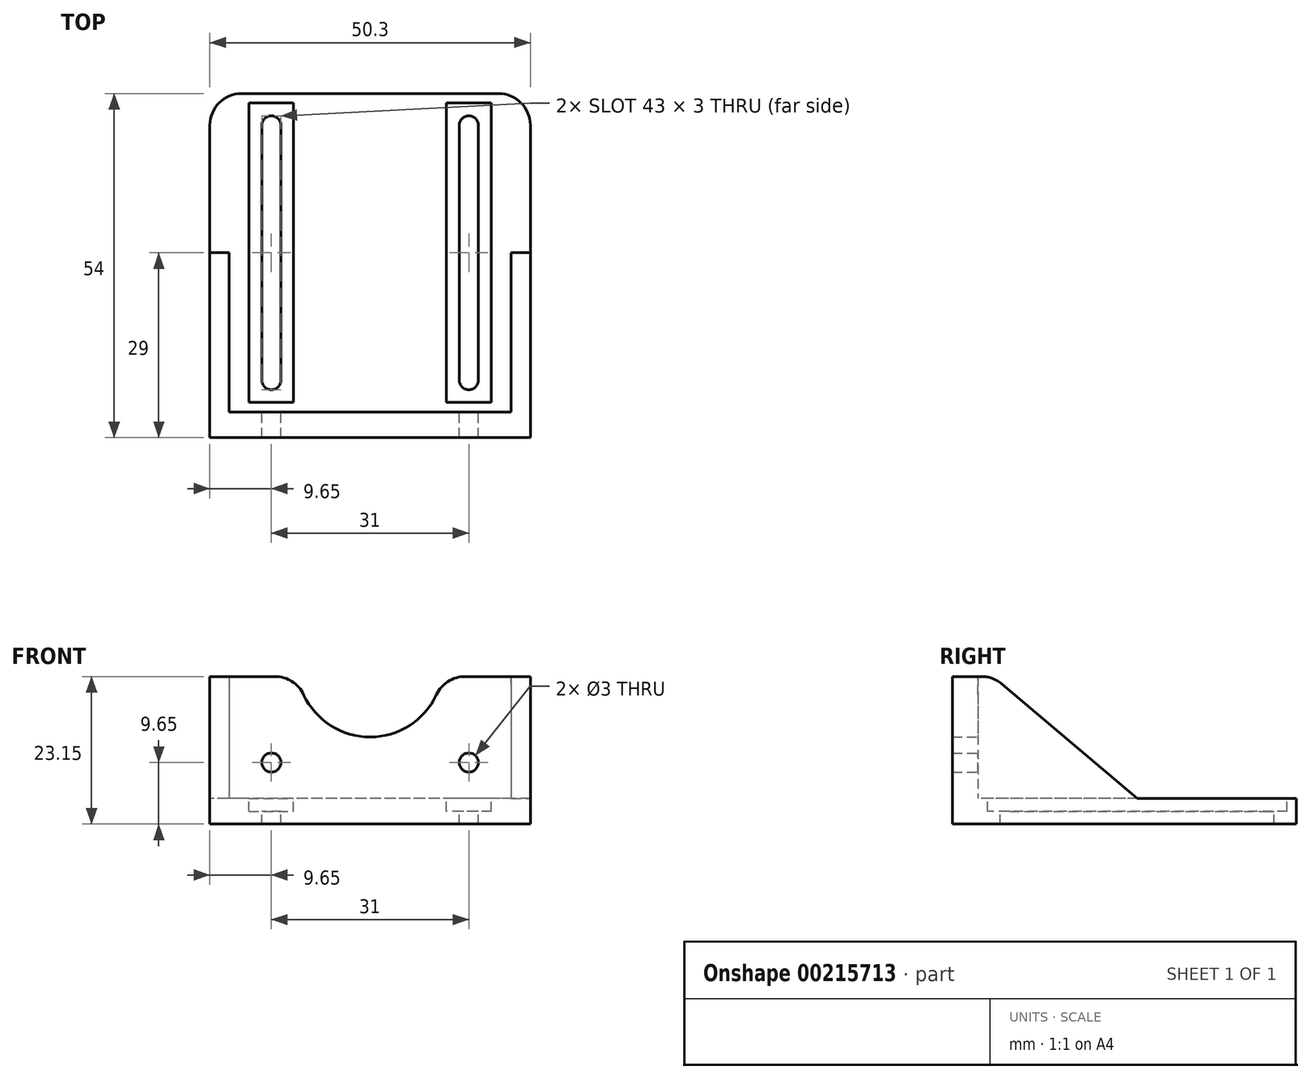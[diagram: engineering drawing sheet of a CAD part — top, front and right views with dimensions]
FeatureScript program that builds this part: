
annotation { "Feature Type Name" : "Feature", "Feature Type Description" : "" }
export const myFeature = defineFeature(function(context is Context, id is Id, definition is map)
    precondition{}
    {
        {
            var Q0;
            Q0=qCreatedBy(makeId("Front.planeOp"),FACE);
            var sketch = newSketch(context, id + "F0", { "sketchPlane" : qUnion([Q0])});
            skLineSegment(sketch, "E0.bottom", {"start": v(-25.15, 42.3) * mm, "end": v(25.15, 42.3) * mm});
            skLineSegment(sketch, "E0.top", {"start": v(-25.15, -4) * mm, "end": v(25.15, -4) * mm});
            skLineSegment(sketch, "E0.left", {"start": v(-25.15, 42.3) * mm, "end": v(-25.15, -4) * mm});
            skLineSegment(sketch, "E0.right", {"start": v(25.15, 42.3) * mm, "end": v(25.15, -4) * mm});
            skCircle(sketch, "E1", {"center": v(-15.5, 36.65) * mm, "radius": 1.5 * mm});
            skCircle(sketch, "E2.MirrorC", {"center": v(15.5, 36.65) * mm, "radius": 1.5 * mm});
            skCircle(sketch, "E3", {"center": v(-15.5, 5.65) * mm, "radius": 1.5 * mm});
            skCircle(sketch, "E4.MirrorC", {"center": v(15.5, 5.65) * mm, "radius": 1.5 * mm});
            skCircle(sketch, "E5", {"center": v(0, 21.15) * mm, "radius": 11.5 * mm});
            skLineSegment(sketch, "E6", {"start": v(-15.5, 36.65) * mm, "end": v(15.5, 5.65) * mm, "construction": true});
            skLineSegment(sketch, "E7", {"start": v(0, 42.3) * mm, "end": v(0, 0) * mm, "construction": true});
            skSolve(sketch);
        }
        {
            var Q0;
            Q0 = qSketchRegion(id + "F0", true);
            extrude(context, id + "F1", {"entities" : qUnion([Q0]), "depth" : 4 * mm});
        }
        {
            var Q0;
            Q0=makeQuery(id+"F1.opExtrude","CAP_FACE",FACE,{"disambiguationData":[OSD([sQuery(id+"F0.wireOp",EDGE,"E0.bottom"),sQuery(id+"F0.wireOp",EDGE,"E0.top"),sQuery(id+"F0.wireOp",EDGE,"E0.left"),sQuery(id+"F0.wireOp",EDGE,"E0.right"),sQuery(id+"F0.wireOp",EDGE,"E1"),sQuery(id+"F0.wireOp",EDGE,"E2.MirrorC"),sQuery(id+"F0.wireOp",EDGE,"E3"),sQuery(id+"F0.wireOp",EDGE,"E4.MirrorC"),sQuery(id+"F0.wireOp",EDGE,"E5")])],"isStart":true});
            var sketch = newSketch(context, id + "F2", { "sketchPlane" : qUnion([Q0])});
            skLineSegment(sketch, "E8.bottom", {"start": v(-25.15, 0) * mm, "end": v(25.15, 0) * mm});
            skLineSegment(sketch, "E8.top", {"start": v(-25.15, -4) * mm, "end": v(25.15, -4) * mm});
            skLineSegment(sketch, "E8.left", {"start": v(-25.15, 0) * mm, "end": v(-25.15, -4) * mm});
            skLineSegment(sketch, "E8.right", {"start": v(25.15, 0) * mm, "end": v(25.15, -4) * mm});
            skSolve(sketch);
        }
        {
            var Q0;
            Q0 = qSketchRegion(id + "F2", true);
            extrude(context, id + "F3", {"entities" : qUnion([Q0]), "operationType" : NewBodyOperationType.ADD, "depth" : 50 * mm});
        }
        {
            var Q0;
            Q0=makeQuery(id+"F3.boolean.opBoolean","MERGE",FACE,{"derivedFrom":[makeQuery(id+"F1.opExtrude","SWEPT_FACE",FACE,{"disambiguationData":[OSD([sQuery(id+"F0.wireOp",EDGE,"E0.right")])]}),makeQuery(id+"F3.opExtrude","SWEPT_FACE",FACE,{"disambiguationData":[OSD([sQuery(id+"F2.wireOp",EDGE,"E8.left")])]})]});
            var sketch = newSketch(context, id + "F4", { "sketchPlane" : qUnion([Q0])});
            skLineSegment(sketch, "E9", {"start": v(0, 21.15) * mm, "end": v(25, 0) * mm});
            skLineSegment(sketch, "E10", {"start": v(25, 0) * mm, "end": v(0, 0) * mm});
            skLineSegment(sketch, "E11", {"start": v(0, 0) * mm, "end": v(0, 21.15) * mm});
            skSolve(sketch);
        }
        {
            var Q0;
            Q0 = qSketchRegion(id + "F4", true);
            extrude(context, id + "F5", {"entities" : qUnion([Q0]), "operationType" : NewBodyOperationType.ADD, "oppositeDirection" : true, "depth" : 3 * mm});
        }
        {
            var Q0;
            Q0=makeQuery(id+"F3.boolean.opBoolean","MERGE",FACE,{"derivedFrom":[makeQuery(id+"F1.opExtrude","SWEPT_FACE",FACE,{"disambiguationData":[OSD([sQuery(id+"F0.wireOp",EDGE,"E0.left")])]}),makeQuery(id+"F3.opExtrude","SWEPT_FACE",FACE,{"disambiguationData":[OSD([sQuery(id+"F2.wireOp",EDGE,"E8.right")])]})]});
            var sketch = newSketch(context, id + "F6", { "sketchPlane" : qUnion([Q0])});
            skLineSegment(sketch, "E12", {"start": v(0, 21.15) * mm, "end": v(-25, 0) * mm});
            skLineSegment(sketch, "E13", {"start": v(-25, 0) * mm, "end": v(0, 0) * mm});
            skLineSegment(sketch, "E14", {"start": v(0, 0) * mm, "end": v(0, 21.15) * mm});
            skSolve(sketch);
        }
        {
            var Q0;
            Q0 = qSketchRegion(id + "F6", true);
            extrude(context, id + "F7", {"entities" : qUnion([Q0]), "operationType" : NewBodyOperationType.ADD, "oppositeDirection" : true, "depth" : 3 * mm});
        }
        {
            var Q0;
            Q0=makeQuery(id+"F3.opExtrude","SWEPT_FACE",FACE,{"disambiguationData":[OSD([sQuery(id+"F2.wireOp",EDGE,"E8.bottom")])]});
            var sketch = newSketch(context, id + "F8", { "sketchPlane" : qUnion([Q0])});
            skLineSegment(sketch, "E15", {"start": v(-15.5, 50) * mm, "end": v(-15.5, 0) * mm, "construction": true});
            skArc(sketch, "E16", {"start": v(-14, 45) * mm, "mid": v(-15.5, 46.5) * mm, "end": v(-17, 45) * mm});
            skArc(sketch, "E17", {"start": v(-17, 5) * mm, "mid": v(-15.5, 3.5) * mm, "end": v(-14, 5) * mm});
            skLineSegment(sketch, "E18", {"start": v(-17, 45) * mm, "end": v(-17, 5) * mm});
            skLineSegment(sketch, "E19", {"start": v(-14, 45) * mm, "end": v(-14, 5) * mm});
            skLineSegment(sketch, "E20.MirrorCS", {"start": v(14, 45) * mm, "end": v(14, 5) * mm});
            skArc(sketch, "E21.MirrorCS", {"start": v(14, 45) * mm, "mid": v(15.5, 46.5) * mm, "end": v(17, 45) * mm});
            skLineSegment(sketch, "E22.MirrorCS", {"start": v(17, 45) * mm, "end": v(17, 5) * mm});
            skArc(sketch, "E23.MirrorCS", {"start": v(17, 5) * mm, "mid": v(15.5, 3.5) * mm, "end": v(14, 5) * mm});
            skSolve(sketch);
        }
        {
            var Q0;
            Q0 = qSketchRegion(id + "F8", true);
            extrude(context, id + "F9", {"entities" : qUnion([Q0]), "operationType" : NewBodyOperationType.REMOVE, "endBound" : BoundingType.THROUGH_ALL, "oppositeDirection" : true, "depth" : 25 * mm});
        }
        {
            var Q0;
            Q0=makeQuery(id+"F3.opExtrude","SWEPT_FACE",FACE,{"disambiguationData":[OSD([sQuery(id+"F2.wireOp",EDGE,"E8.bottom")])]});
            var sketch = newSketch(context, id + "F10", { "sketchPlane" : qUnion([Q0])});
            skLineSegment(sketch, "E24.bottom", {"start": v(-19, 48.5) * mm, "end": v(-12, 48.5) * mm});
            skLineSegment(sketch, "E24.top", {"start": v(-19, 1.5) * mm, "end": v(-12, 1.5) * mm});
            skLineSegment(sketch, "E24.left", {"start": v(-19, 48.5) * mm, "end": v(-19, 1.5) * mm});
            skLineSegment(sketch, "E24.right", {"start": v(-12, 48.5) * mm, "end": v(-12, 1.5) * mm});
            skLineSegment(sketch, "E25.MirrorCS", {"start": v(12, 48.5) * mm, "end": v(12, 1.5) * mm});
            skLineSegment(sketch, "E26.MirrorCS", {"start": v(19, 48.5) * mm, "end": v(12, 48.5) * mm});
            skLineSegment(sketch, "E27.MirrorCS", {"start": v(19, 48.5) * mm, "end": v(19, 1.5) * mm});
            skLineSegment(sketch, "E28.MirrorCS", {"start": v(19, 1.5) * mm, "end": v(12, 1.5) * mm});
            skSolve(sketch);
        }
        {
            var Q0;
            Q0 = qSketchRegion(id + "F10", true);
            extrude(context, id + "F11", {"entities" : qUnion([Q0]), "operationType" : NewBodyOperationType.REMOVE, "oppositeDirection" : true, "depth" : 2 * mm});
        }
        {
            var Q0;
            Q0=makeQuery(id+"F1.opExtrude","CAP_FACE",FACE,{"disambiguationData":[OSD([sQuery(id+"F0.wireOp",EDGE,"E0.bottom"),sQuery(id+"F0.wireOp",EDGE,"E0.top"),sQuery(id+"F0.wireOp",EDGE,"E0.left"),sQuery(id+"F0.wireOp",EDGE,"E0.right"),sQuery(id+"F0.wireOp",EDGE,"E1"),sQuery(id+"F0.wireOp",EDGE,"E2.MirrorC"),sQuery(id+"F0.wireOp",EDGE,"E3"),sQuery(id+"F0.wireOp",EDGE,"E4.MirrorC"),sQuery(id+"F0.wireOp",EDGE,"E5")])],"isStart":false});
            var sketch = newSketch(context, id + "F12", { "sketchPlane" : qUnion([Q0])});
            skLineSegment(sketch, "E29.bottom", {"start": v(-25.15, 42.3) * mm, "end": v(25.15, 42.3) * mm});
            skLineSegment(sketch, "E29.top", {"start": v(-25.15, 19.15) * mm, "end": v(25.15, 19.15) * mm});
            skLineSegment(sketch, "E29.left", {"start": v(-25.15, 42.3) * mm, "end": v(-25.15, 19.15) * mm});
            skLineSegment(sketch, "E29.right", {"start": v(25.15, 42.3) * mm, "end": v(25.15, 19.15) * mm});
            skSolve(sketch);
        }
        {
            var Q0;
            Q0 = qSketchRegion(id + "F12", true);
            extrude(context, id + "F13", {"entities" : qUnion([Q0]), "operationType" : NewBodyOperationType.REMOVE, "endBound" : BoundingType.THROUGH_ALL, "oppositeDirection" : true, "depth" : 25 * mm});
        }
        {
            var Q0;
            Q0=makeQuery(id+"F13.boolean.opBoolean","INTERSECT",EDGE,{"derivedFrom":[makeQuery(id+"F5.opExtrude","SWEPT_FACE",FACE,{"disambiguationData":[OSD([sQuery(id+"F4.wireOp",EDGE,"E9")])]}),makeQuery(id+"F13.opExtrude","SWEPT_FACE",FACE,{"disambiguationData":[OSD([sQuery(id+"F12.wireOp",EDGE,"E29.top")])]})]});
            var Q1;
            Q1=makeQuery(id+"F13.boolean.opBoolean","INTERSECT",EDGE,{"derivedFrom":[makeQuery(id+"F7.opExtrude","SWEPT_FACE",FACE,{"disambiguationData":[OSD([sQuery(id+"F6.wireOp",EDGE,"E12")])]}),makeQuery(id+"F13.opExtrude","SWEPT_FACE",FACE,{"disambiguationData":[OSD([sQuery(id+"F12.wireOp",EDGE,"E29.top")])]})]});
            var Q2;
            Q2=makeQuery(id+"F13.boolean.opBoolean","INTERSECT",EDGE,{"disambiguationData":[OD(0.0)],"derivedFrom":[makeQuery(id+"F1.opExtrude","SWEPT_FACE",FACE,{"disambiguationData":[OSD([sQuery(id+"F0.wireOp",EDGE,"E5")])]}),makeQuery(id+"F13.opExtrude","SWEPT_FACE",FACE,{"disambiguationData":[OSD([sQuery(id+"F12.wireOp",EDGE,"E29.top")])]})]});
            var Q3;
            Q3=makeQuery(id+"F13.boolean.opBoolean","INTERSECT",EDGE,{"disambiguationData":[OD(1.0)],"derivedFrom":[makeQuery(id+"F1.opExtrude","SWEPT_FACE",FACE,{"disambiguationData":[OSD([sQuery(id+"F0.wireOp",EDGE,"E5")])]}),makeQuery(id+"F13.opExtrude","SWEPT_FACE",FACE,{"disambiguationData":[OSD([sQuery(id+"F12.wireOp",EDGE,"E29.top")])]})]});
            var Q4;
            Q4=makeQuery(id+"F5.opExtrude","SWEPT_EDGE",EDGE,{"disambiguationData":[OSD([sQuery(id+"F0.wireOp",EDGE,"E0.right"),sQuery(id+"F2.wireOp",EDGE,"E8.bottom"),sQuery(id+"F2.wireOp",EDGE,"E8.left"),sQuery(id+"F4.wireOp",EDGE,"E9"),sQuery(id+"F4.wireOp",EDGE,"E10")])]});
            var Q5;
            Q5=makeQuery(id+"F7.opExtrude","SWEPT_EDGE",EDGE,{"disambiguationData":[OSD([sQuery(id+"F0.wireOp",EDGE,"E0.left"),sQuery(id+"F2.wireOp",EDGE,"E8.bottom"),sQuery(id+"F2.wireOp",EDGE,"E8.right"),sQuery(id+"F6.wireOp",EDGE,"E12"),sQuery(id+"F6.wireOp",EDGE,"E13")])]});
            var Q6;
            Q6=makeQuery(id+"F3.opExtrude","CAP_EDGE",EDGE,{"disambiguationData":[OSD([sQuery(id+"F2.wireOp",EDGE,"E8.left")])],"isStart":false});
            var Q7;
            Q7=makeQuery(id+"F3.opExtrude","CAP_EDGE",EDGE,{"disambiguationData":[OSD([sQuery(id+"F2.wireOp",EDGE,"E8.right")])],"isStart":false});
            fillet(context, id + "F14", {"entities" : qUnion([Q0, Q1, Q2, Q3, Q4, Q5, Q6, Q7]), "radius" : 5 * mm, "tangentPropagation" : true, "allowEdgeOverflow" : false});
        }
    });
